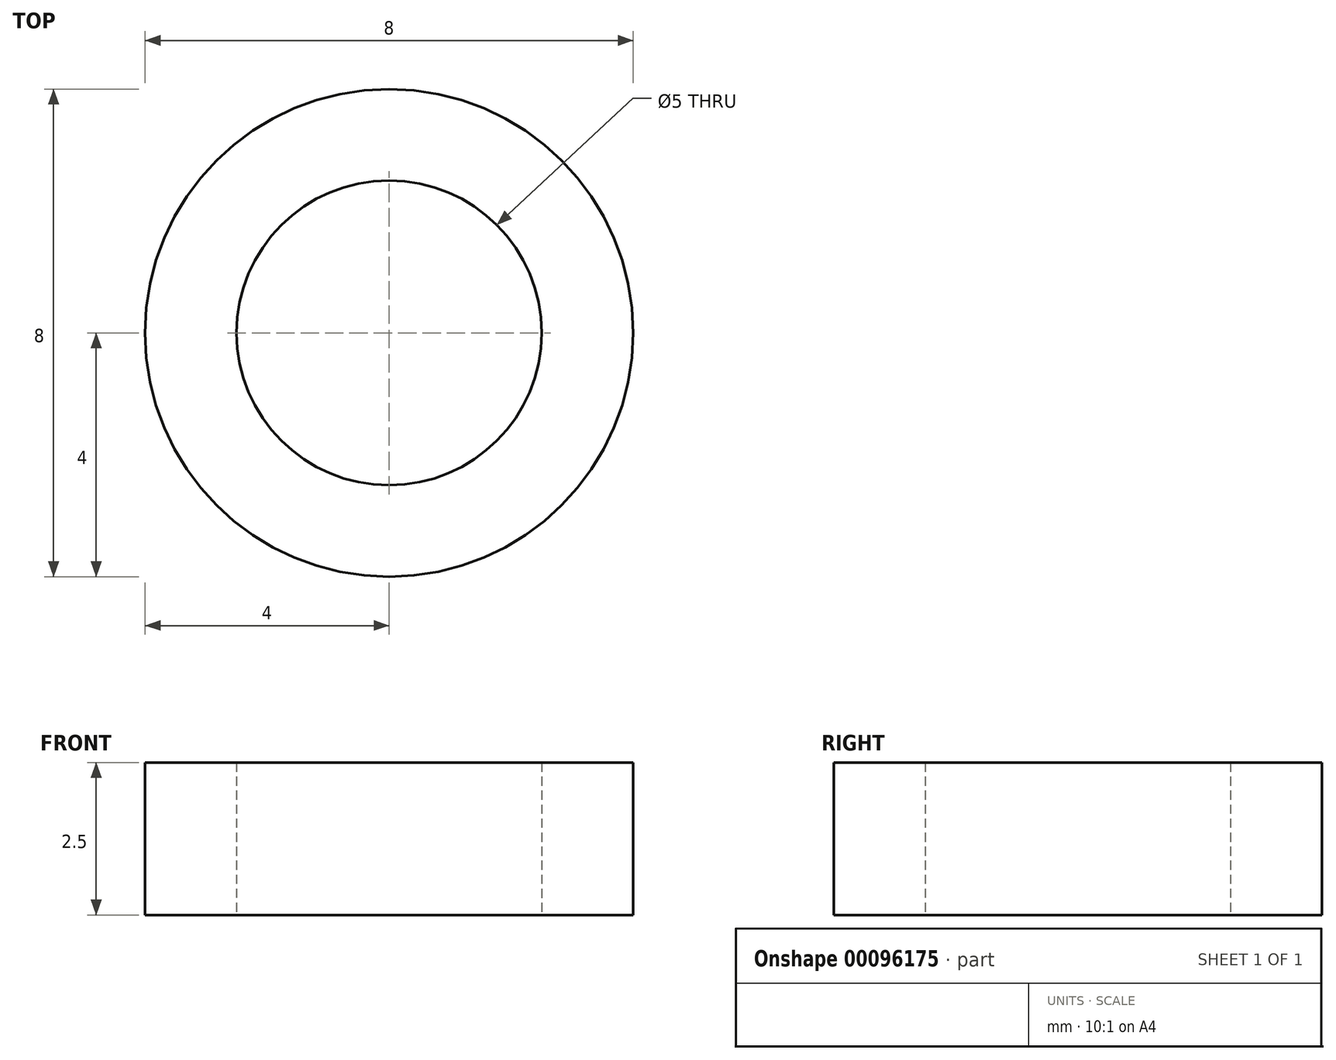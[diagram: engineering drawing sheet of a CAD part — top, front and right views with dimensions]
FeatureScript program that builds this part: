
annotation { "Feature Type Name" : "Feature", "Feature Type Description" : "" }
export const myFeature = defineFeature(function(context is Context, id is Id, definition is map)
    precondition{}
    {
        {
            var Q0;
            Q0=qCreatedBy(makeId("Top.planeOp"),FACE);
            var sketch = newSketch(context, id + "F0", { "sketchPlane" : qUnion([Q0])});
            skCircle(sketch, "E0", {"center": v(0, 0) * mm, "radius": 2.5 * mm});
            skCircle(sketch, "E1", {"center": v(0, 0) * mm, "radius": 4 * mm});
            skSolve(sketch);
        }
        {
            var Q0;
            Q0 = qSketchRegion(id + "F0", true);
            extrude(context, id + "F1", {"entities" : qUnion([Q0]), "depth" : 2.5 * mm});
        }
    });
